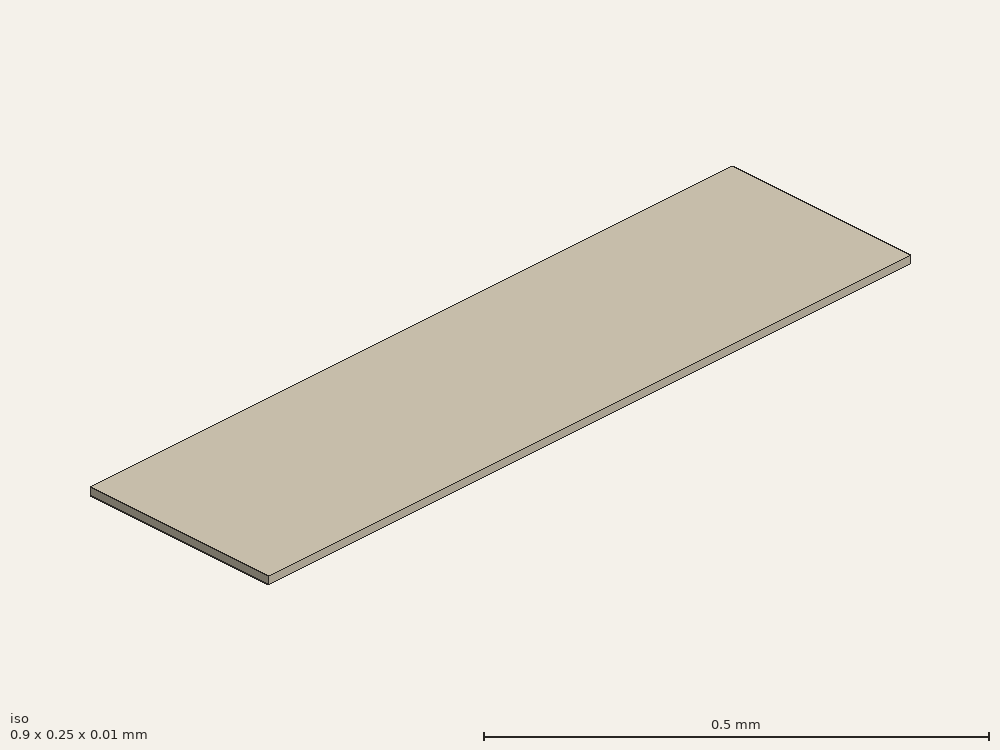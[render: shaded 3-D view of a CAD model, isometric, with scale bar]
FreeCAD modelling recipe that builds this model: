
FCSTD DOCUMENT
Label: insertion_face
objects: Sketcher::SketchObject×1, PartDesign::Pad×1
note: 3 computed .brp shape members not serialized (recipe doc carries the construction recipe); baked Part::Feature solids carry a one-line shape summary decoded from their .brp

FEATURE [Sketcher::SketchObject] Sketch
  sketch-geometry (4):
    g0: LineSegment StartX=-0.45 StartY=-0.4 StartZ=0 EndX=0.45 EndY=-0.4 EndZ=0
    g1: LineSegment StartX=0.45 StartY=-0.4 StartZ=0 EndX=0.45 EndY=-0.65 EndZ=0
    g2: LineSegment StartX=0.45 StartY=-0.65 StartZ=0 EndX=-0.45 EndY=-0.65 EndZ=0
    g3: LineSegment StartX=-0.45 StartY=-0.65 StartZ=0 EndX=-0.45 EndY=-0.4 EndZ=0
  constraints (12):
    c: Coincident(g0,g1)
    c: Coincident(g1,g2)
    c: Coincident(g2,g3)
    c: Coincident(g3,g0)
    c: Horizontal(g0)
    c: Horizontal(g2)
    c: Vertical(g1)
    c: Vertical(g3)
    c: DistanceX(g0) = 0.45
    c: DistanceY(g0) = -0.4
    c: DistanceX(g2) = -0.45
    c: DistanceY(g2) = -0.65
FEATURE [PartDesign::Pad] Pad
  Length = 0.01
  MirroredExtent = false
  Sketch = -> Sketch
